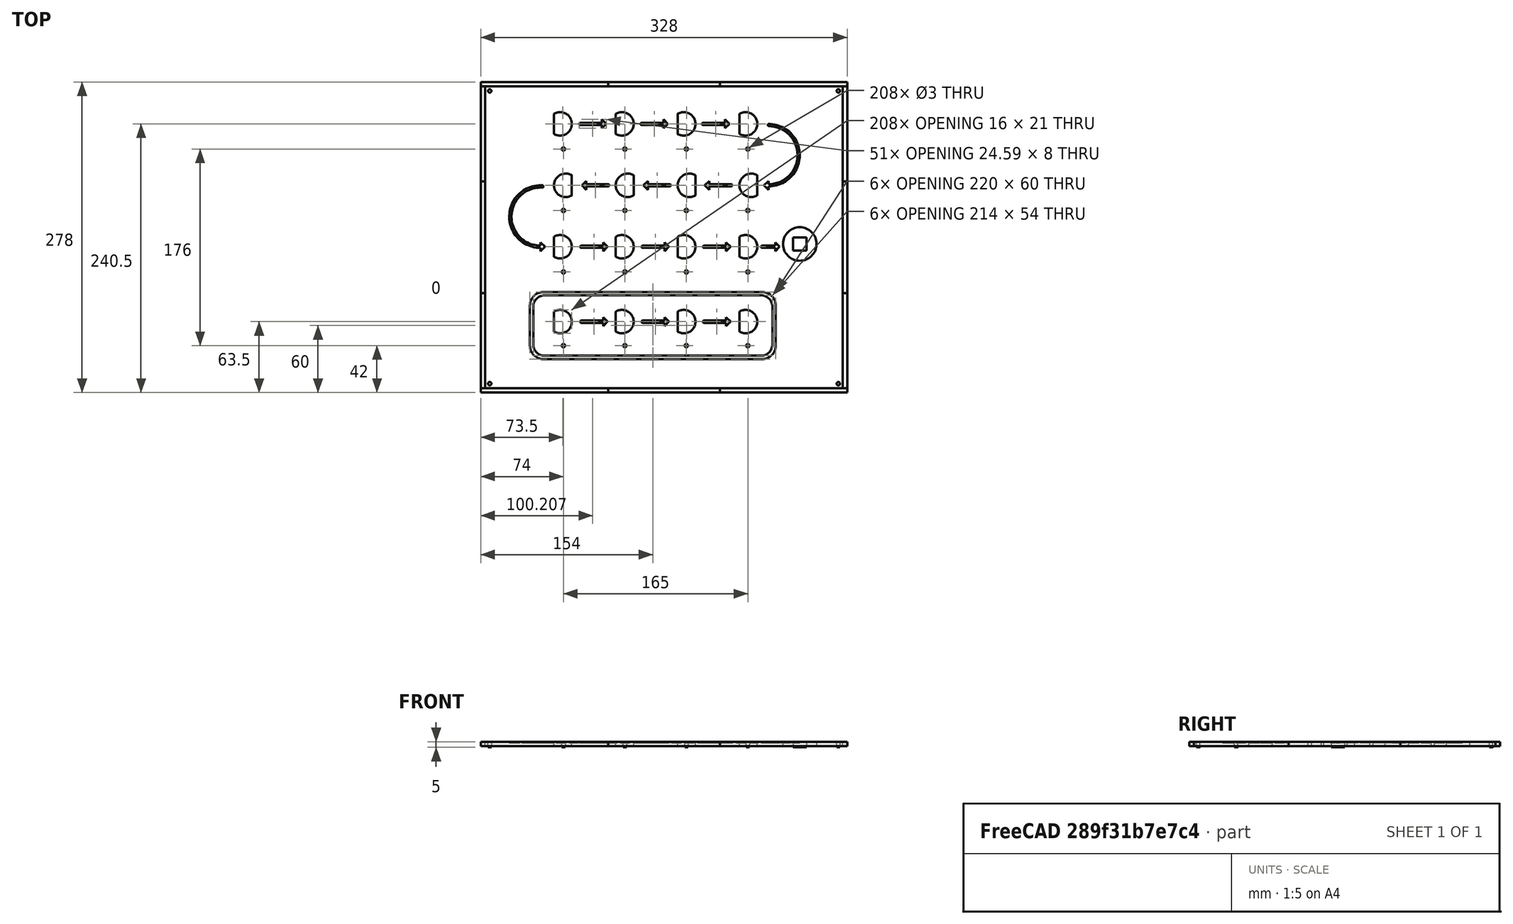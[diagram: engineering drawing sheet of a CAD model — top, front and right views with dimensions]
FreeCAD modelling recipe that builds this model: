
FCSTD DOCUMENT  (FreeCAD 0.14R3700 (Git))
Label: interFace-4mm (1)
License: CC-BY 3.0
LicenseURL: http://creativecommons.org/licenses/by/3.0/
objects: Sketcher::SketchObject×25, PartDesign::Pocket×17, PartDesign::Pad×8, Part::Cut×7, PartDesign::Fillet×7, PartDesign::LinearPattern×5, Part::Offset×4, Part::FeaturePython×4, Part::Box×3, Part::Fillet×2, Mesh::Feature×1
note: 107 computed .brp shape members not serialized (recipe doc carries the construction recipe); baked Part::Feature solids carry a one-line shape summary decoded from their .brp

FEATURE [Part::Box] Box  label="Cubo"
  Height = 4
  Length = 320
  Width = 270
FEATURE [Sketcher::SketchObject] Sketch004
  ExternalGeometry = -> [Box]
  Placement = pos=(0,0,4) rot=(0,0,1;0rad)
  Support = -> Box [Face6]
  sketch-geometry (4):
    g0: Circle CenterX=70 CenterY=214 CenterZ=0 NormalX=0 NormalY=0 NormalZ=1 Radius=1.5
    g1: Circle CenterX=125 CenterY=214 CenterZ=0 NormalX=0 NormalY=0 NormalZ=1 Radius=1.5
    g2: Circle CenterX=180 CenterY=214 CenterZ=0 NormalX=0 NormalY=0 NormalZ=1 Radius=1.5
    g3: Circle CenterX=235 CenterY=214 CenterZ=0 NormalX=0 NormalY=0 NormalZ=1 Radius=1.5
  constraints (12):
    c: Equal(g0,g1)
    c: Equal(g1,g3)
    c: Radius(g3) = 1.5
    c: DistanceY(g0,g-3) = 56
    c: DistanceY(g1,g-3) = 56
    c: DistanceX(g0,g-3) = -70
    c: DistanceX(g0,g1) = 55
    c: DistanceX(g1,g2) = 55
    c: DistanceX(g2,g3) = 55
    c: DistanceY(g3,g-3) = 56
    c: DistanceY(g2,g-3) = 56
    c: Equal(g2,g3)
FEATURE [Sketcher::SketchObject] Sketch008
  Placement = pos=(57,251.5,-1) rot=(0,0,-1;1.5708rad)
  sketch-geometry (2):
    g0: ArcOfCircle CenterX=15 CenterY=10 CenterZ=0 NormalX=0 NormalY=0 NormalZ=1 Radius=10 StartAngle=5.75959 EndAngle=9.94838
    g1: LineSegment StartX=6.33975 StartY=5 StartZ=0 EndX=23.6603 EndY=5 EndZ=0
  constraints (7):
    c: Radius(g0) = 10
    c: Horizontal(g1)
    c: PointOnObject(g0,g1)
    c: PointOnObject(g0,g1)
    c: Coincident(g1,g0)
    c: Coincident(g1,g0)
    c: DistanceY(g0,g0) = 5
FEATURE [PartDesign::Pad] Pad
  Length = 7
  Length2 = 100
  Placement = pos=(57,251.5,-1) rot=(0,0,-1;1.5708rad)
  Sketch = -> Sketch008
  Type = 0
FEATURE [Mesh::Feature] fichaLab3y  label="fichaLab3y4"
  Placement = pos=(127.33,181.5,-0.5) rot=(0,0,1;0rad)
FEATURE [PartDesign::Pocket] Pocket
  Length = 5
  Sketch = -> Sketch004
  Type = 0
FEATURE [PartDesign::LinearPattern] LinearPattern
  Direction = -> Sketch004 [V_Axis]
  Length = 110
  Occurrences = 3
  Originals = -> [Pocket]
  Reversed = true
FEATURE [Sketcher::SketchObject] Sketch005
  Placement = pos=(0,0,4) rot=(0,0,1;0rad)
  Support = -> LinearPattern [Face3]
  sketch-geometry (4):
    g0: Circle CenterX=70 CenterY=38 CenterZ=0 NormalX=0 NormalY=0 NormalZ=1 Radius=1.5
    g1: Circle CenterX=125 CenterY=38 CenterZ=0 NormalX=0 NormalY=0 NormalZ=1 Radius=1.5
    g2: Circle CenterX=180 CenterY=38 CenterZ=0 NormalX=0 NormalY=0 NormalZ=1 Radius=1.5
    g3: Circle CenterX=235 CenterY=38 CenterZ=0 NormalX=0 NormalY=0 NormalZ=1 Radius=1.5
  constraints (12):
    c: Equal(g0,g1)
    c: Equal(g1,g2)
    c: Equal(g2,g3)
    c: Radius(g0) = 1.5
    c: DistanceX(g-1,g0) = 70
    c: DistanceY(g-1,g0) = 38
    c: DistanceX(g0,g1) = 55
    c: DistanceY(g-1,g1) = 38
    c: DistanceX(g2,g1) = -55
    c: DistanceY(g-1,g2) = 38
    c: DistanceY(g-1,g3) = 38
    c: DistanceX(g3,g2) = -55
FEATURE [PartDesign::Pocket] Pocket001
  Length = 5
  Sketch = -> Sketch005
  Type = 0
FEATURE [Sketcher::SketchObject] Sketch007
  Placement = pos=(0,0,4) rot=(0,0,1;0rad)
  Support = -> Pocket001 [Face3]
  sketch-geometry (16):
    g0: Circle CenterX=67 CenterY=236.5 CenterZ=0 NormalX=0 NormalY=0 NormalZ=1 Radius=2
    g1: Circle CenterX=122.333 CenterY=236.5 CenterZ=0 NormalX=0 NormalY=0 NormalZ=1 Radius=2
    g2: Circle CenterX=177.667 CenterY=236.5 CenterZ=0 NormalX=0 NormalY=0 NormalZ=1 Radius=2
    g3: Circle CenterX=233 CenterY=236.5 CenterZ=0 NormalX=0 NormalY=0 NormalZ=1 Radius=2
    g4: Circle CenterX=72 CenterY=181.5 CenterZ=0 NormalX=0 NormalY=0 NormalZ=1 Radius=2
    g5: Circle CenterX=127.333 CenterY=181.5 CenterZ=0 NormalX=0 NormalY=0 NormalZ=1 Radius=2
    g6: Circle CenterX=182.667 CenterY=181.5 CenterZ=0 NormalX=0 NormalY=0 NormalZ=1 Radius=2
    g7: Circle CenterX=238 CenterY=181.5 CenterZ=0 NormalX=0 NormalY=0 NormalZ=1 Radius=2
    g8: Circle CenterX=67 CenterY=126.5 CenterZ=0 NormalX=0 NormalY=0 NormalZ=1 Radius=2
    g9: Circle CenterX=122.333 CenterY=126.5 CenterZ=0 NormalX=0 NormalY=0 NormalZ=1 Radius=2
    g10: Circle CenterX=177.667 CenterY=126.5 CenterZ=0 NormalX=0 NormalY=0 NormalZ=1 Radius=2
    g11: Circle CenterX=233 CenterY=126.5 CenterZ=0 NormalX=0 NormalY=0 NormalZ=1 Radius=2
    g12: Circle CenterX=67 CenterY=59.5 CenterZ=0 NormalX=0 NormalY=0 NormalZ=1 Radius=2
    g13: Circle CenterX=122.333 CenterY=59.5 CenterZ=0 NormalX=0 NormalY=0 NormalZ=1 Radius=2
    g14: Circle CenterX=177.667 CenterY=59.5 CenterZ=0 NormalX=0 NormalY=0 NormalZ=1 Radius=2
    g15: Circle CenterX=233 CenterY=59.5 CenterZ=0 NormalX=0 NormalY=0 NormalZ=1 Radius=2
  constraints (28):
    c: Equal(g0,g1)
    c: Equal(g1,g3)
    c: Equal(g3,g2)
    c: Radius(g0) = 2
    c: Equal(g7,g6)
    c: Equal(g6,g5)
    c: Equal(g5,g4)
    c: Radius(g7) = 2
    c: Equal(g11,g10)
    c: Equal(g10,g9)
    c: Equal(g9,g8)
    c: Radius(g11) = 2
    c: Equal(g15,g14)
    c: Equal(g14,g13)
    c: Equal(g13,g12)
    c: Radius(g15) = 2
    c: DistanceX(g0,g1) = 55.3333
    c: DistanceX(g1,g2) = 55.3334
    c: DistanceX(g2,g3) = 55.3333
    c: DistanceX(g4,g5) = 55.3333
    c: DistanceX(g5,g6) = 55.3334
    c: DistanceX(g6,g7) = 55.3333
    c: DistanceX(g8,g9) = 55.3333
    c: DistanceX(g9,g10) = 55.3334
    c: DistanceX(g10,g11) = 55.3333
    c: DistanceX(g12,g13) = 55.3333
    c: DistanceX(g13,g14) = 55.3333
    c: DistanceX(g14,g15) = 55.3334
FEATURE [PartDesign::Pocket] Pocket002
  Length = 5
  Sketch = -> Sketch007
  Type = 0
FEATURE [Part::Offset] Offset
  Fill = false
  Intersection = false
  Join = 0
  Mode = 0
  SelfIntersection = false
  Source = -> Pad
  Value = 0.5
FEATURE [Part::FeaturePython] Array  # Draft array (typed FeaturePython)
  Angle = 360
  ArrayType = 0
  Axis = (0,0,1)
  Base = -> Offset
  Center = (0,0,0)
  IntervalX = (55.33,0,0)
  IntervalY = (0,1,0)
  IntervalZ = (0,0,1)
  NumberPolar = 1
  NumberX = 4
  NumberY = 1
  NumberZ = 1
FEATURE [Part::Cut] Cut
  Base = -> Pocket002
  Tool = -> Array
FEATURE [Sketcher::SketchObject] Sketch
  Placement = pos=(57,141.5,-1) rot=(0,0,-1;1.5708rad)
  sketch-geometry (2):
    g0: ArcOfCircle CenterX=15 CenterY=10 CenterZ=0 NormalX=0 NormalY=0 NormalZ=1 Radius=10 StartAngle=5.75959 EndAngle=9.94838
    g1: LineSegment StartX=6.33975 StartY=5 StartZ=0 EndX=23.6603 EndY=5 EndZ=0
  constraints (7):
    c: Radius(g0) = 10
    c: Horizontal(g1)
    c: PointOnObject(g0,g1)
    c: PointOnObject(g0,g1)
    c: Coincident(g1,g0)
    c: Coincident(g1,g0)
    c: DistanceY(g0,g0) = 5
FEATURE [PartDesign::Pad] Pad001
  Length = 7
  Length2 = 100
  Placement = pos=(57,141.5,-1) rot=(0,0,-1;1.5708rad)
  Sketch = -> Sketch
  Type = 0
FEATURE [Part::Offset] Offset001
  Fill = false
  Intersection = false
  Join = 0
  Mode = 0
  SelfIntersection = false
  Source = -> Pad001
  Value = 0.5
FEATURE [Part::FeaturePython] Array001  # Draft array (typed FeaturePython)
  Angle = 360
  ArrayType = 0
  Axis = (0,0,1)
  Base = -> Offset001
  Center = (0,0,0)
  IntervalX = (55.33,0,0)
  IntervalY = (0,1,0)
  IntervalZ = (0,0,1)
  NumberPolar = 1
  NumberX = 4
  NumberY = 1
  NumberZ = 1
FEATURE [Part::Cut] Cut001
  Base = -> Cut
  Tool = -> Array001
FEATURE [Sketcher::SketchObject] Sketch009
  Placement = pos=(57,74.5,-1) rot=(0,0,-1;1.5708rad)
  sketch-geometry (2):
    g0: ArcOfCircle CenterX=15 CenterY=10 CenterZ=0 NormalX=0 NormalY=0 NormalZ=1 Radius=10 StartAngle=5.75959 EndAngle=9.94838
    g1: LineSegment StartX=6.33975 StartY=5 StartZ=0 EndX=23.6603 EndY=5 EndZ=0
  constraints (7):
    c: Radius(g0) = 10
    c: Horizontal(g1)
    c: PointOnObject(g0,g1)
    c: PointOnObject(g0,g1)
    c: Coincident(g1,g0)
    c: Coincident(g1,g0)
    c: DistanceY(g0,g0) = 5
FEATURE [PartDesign::Pad] Pad002
  Length = 7
  Length2 = 100
  Placement = pos=(57,74.5,-1) rot=(0,0,-1;1.5708rad)
  Sketch = -> Sketch009
  Type = 0
FEATURE [Part::Offset] Offset002
  Fill = false
  Intersection = false
  Join = 0
  Mode = 0
  SelfIntersection = false
  Source = -> Pad002
  Value = 0.5
FEATURE [Part::FeaturePython] Array002  # Draft array (typed FeaturePython)
  Angle = 360
  ArrayType = 0
  Axis = (0,0,1)
  Base = -> Offset002
  Center = (0,0,0)
  IntervalX = (55.33,0,0)
  IntervalY = (0,1,0)
  IntervalZ = (0,0,1)
  NumberPolar = 1
  NumberX = 4
  NumberY = 1
  NumberZ = 1
FEATURE [Part::Cut] Cut002
  Base = -> Cut001
  Tool = -> Array002
FEATURE [Sketcher::SketchObject] Sketch010
  Placement = pos=(82,166.5,-1) rot=(0,0,1;1.5708rad)
  sketch-geometry (2):
    g0: ArcOfCircle CenterX=15 CenterY=10 CenterZ=0 NormalX=0 NormalY=0 NormalZ=1 Radius=10 StartAngle=5.75959 EndAngle=9.94838
    g1: LineSegment StartX=6.33975 StartY=5 StartZ=0 EndX=23.6603 EndY=5 EndZ=0
  constraints (7):
    c: Radius(g0) = 10
    c: Horizontal(g1)
    c: PointOnObject(g0,g1)
    c: PointOnObject(g0,g1)
    c: Coincident(g1,g0)
    c: Coincident(g1,g0)
    c: DistanceY(g0,g0) = 5
FEATURE [PartDesign::Pad] Pad003
  Length = 7
  Length2 = 100
  Placement = pos=(82,166.5,-1) rot=(0,0,1;1.5708rad)
  Sketch = -> Sketch010
  Type = 0
FEATURE [Part::Offset] Offset003
  Fill = false
  Intersection = false
  Join = 0
  Mode = 0
  SelfIntersection = false
  Source = -> Pad003
  Value = 0.5
FEATURE [Part::FeaturePython] Array003  # Draft array (typed FeaturePython)
  Angle = 360
  ArrayType = 0
  Axis = (0,0,1)
  Base = -> Offset003
  Center = (0,0,0)
  IntervalX = (55.33,0,0)
  IntervalY = (0,1,0)
  IntervalZ = (0,0,1)
  NumberPolar = 1
  NumberX = 4
  NumberY = 1
  NumberZ = 1
FEATURE [Part::Cut] Cut003
  Base = -> Cut002
  Tool = -> Array003
FEATURE [Sketcher::SketchObject] Sketch011
  ExternalGeometry = -> [Cut003]
  Placement = pos=(0,0,4) rot=(0,0,1;0rad)
  Support = -> Cut003 [Face3]
  sketch-geometry (4):
    g0: LineSegment StartX=275.5 StartY=135 StartZ=0 EndX=287.5 EndY=135 EndZ=0
    g1: LineSegment StartX=287.5 StartY=135 StartZ=0 EndX=287.5 EndY=123 EndZ=0
    g2: LineSegment StartX=287.5 StartY=123 StartZ=0 EndX=275.5 EndY=123 EndZ=0
    g3: LineSegment StartX=275.5 StartY=123 StartZ=0 EndX=275.5 EndY=135 EndZ=0
  constraints (14):
    c: Coincident(g0,g1)
    c: Coincident(g1,g2)
    c: Coincident(g2,g3)
    c: Coincident(g3,g0)
    c: Horizontal(g0)
    c: Horizontal(g2)
    c: Vertical(g1)
    c: Vertical(g3)
    c: Equal(g0,g2)
    c: Equal(g2,g1)
    c: Equal(g1,g3)
    c: DistanceX(g0) = 12
    c: DistanceX(g1,g-3) = 32.5
    c: DistanceY(g1,g-3) = -123
FEATURE [PartDesign::Pocket] Pocket003  label="interFace-4mm(1)"
  Length = 5
  Sketch = -> Sketch011
  Type = 0
FEATURE [Sketcher::SketchObject] Sketch012
  Placement = pos=(0,0,4) rot=(0,0,1;0rad)
  Support = -> Pocket003 [Face3]
  sketch-geometry (1):
    g0: Circle CenterX=281.5 CenterY=129 CenterZ=0 NormalX=0 NormalY=0 NormalZ=1 Radius=15
  constraints (1):
    c: Radius(g0) = 15
FEATURE [PartDesign::Pocket] Pocket004
  Length = 5
  Sketch = -> Sketch012
  Type = 0
FEATURE [Part::Box] Box001  label="Cubo001"
  Height = 10
  Length = 214
  Placement = pos=(43,29,-2) rot=(0,0,1;0rad)
  Width = 54
FEATURE [Part::Box] Box002  label="Cubo002"
  Height = 10
  Length = 220
  Placement = pos=(40,26,-2) rot=(0,0,1;0rad)
  Width = 60
FEATURE [Part::Cut] Cut004
  Base = -> Box002
  Tool = -> Box001
FEATURE [Part::Fillet] Fillet
  Base = -> Cut004
  Edges = 4 edges r=10: [Edge21,Edge22,Edge23,Edge24]
FEATURE [Part::Fillet] Fillet001
  Base = -> Fillet
  Edges = 4 edges r=12: [Edge29,Edge30,Edge33,Edge35]
  Placement = pos=(0,0,5) rot=(0,0,1;0rad)
FEATURE [Part::Cut] Cut005
  Base = -> Pocket004
  Tool = -> Fillet001
FEATURE [Sketcher::SketchObject] Sketch013
  ExternalGeometry = -> [Cut005]
  Placement = pos=(0,0,4) rot=(0,0,1;0rad)
  Support = -> Cut005 [Face3]
  sketch-geometry (9):
    g0: LineSegment StartX=84.5 StartY=235.5 StartZ=0 EndX=104.5 EndY=235.5 EndZ=0
    g1: LineSegment StartX=104.5 StartY=235.5 StartZ=0 EndX=104.5 EndY=232.5 EndZ=0
    g2: LineSegment StartX=104.5 StartY=232.5 StartZ=0 EndX=108.5 EndY=236.5 EndZ=0
    g3: LineSegment StartX=108.5 StartY=236.5 StartZ=0 EndX=104.5 EndY=240.5 EndZ=0
    g4: LineSegment StartX=104.5 StartY=240.5 StartZ=0 EndX=104.5 EndY=237.5 EndZ=0
    g5: LineSegment StartX=104.5 StartY=237.5 StartZ=0 EndX=84.5 EndY=237.5 EndZ=0
    g6: LineSegment StartX=84.5 StartY=237.5 StartZ=0 EndX=83.5 EndY=236.5 EndZ=0
    g7: LineSegment StartX=83.5 StartY=236.5 StartZ=0 EndX=84.5 EndY=235.5 EndZ=0
    g8: LineSegment [constr] StartX=83.5 StartY=236.5 StartZ=0 EndX=108.5 EndY=236.5 EndZ=0
  constraints (28):
    c: Horizontal(g0)
    c: Coincident(g0,g1)
    c: Vertical(g1)
    c: Coincident(g1,g2)
    c: Coincident(g2,g3)
    c: Coincident(g3,g4)
    c: Coincident(g4,g5)
    c: Horizontal(g5)
    c: DistanceX(g0) = 20
    c: Equal(g5,g0)
    c: DistanceX(g2,g0) = -24
    c: DistanceY(g2,g5) = 1
    c: Equal(g1,g4)
    c: Vertical(g4)
    c: Angle(g3,g2) = 1.5708
    c: DistanceX(g0,g-3) = -23
    c: Coincident(g5,g6)
    c: Coincident(g6,g7)
    c: Coincident(g7,g0)
    c: Coincident(g8,g6)
    c: Coincident(g8,g2)
    c: Horizontal(g8)
    c: Equal(g6,g7)
    c: Equal(g0,g5)
    c: Equal(g2,g3)
    c: Equal(g1,g4)
    c: Symmetric(g-3,g-3,g8)
    c: DistanceX(g6,g0) = 1
FEATURE [PartDesign::Pocket] Pocket005
  Length = 1
  Sketch = -> Sketch013
  Type = 0
FEATURE [PartDesign::LinearPattern] LinearPattern001
  Direction = -> Sketch013 [H_Axis]
  Length = 110
  Occurrences = 3
  Originals = -> [Pocket005]
FEATURE [Part::Cut] Cut006
  Base = -> Pocket004
  Tool = -> Fillet001
FEATURE [PartDesign::Fillet] Fillet002
  Base = -> LinearPattern001 [Edge239,Edge234,Edge218]
  Radius = 1
FEATURE [Sketcher::SketchObject] Sketch014
  ExternalGeometry = -> [Fillet002]
  Placement = pos=(0,0,4) rot=(0,0,1;0rad)
  Support = -> Fillet002 [Face1]
  sketch-geometry (9):
    g0: LineSegment StartX=220.49 StartY=182.5 StartZ=0 EndX=200.49 EndY=182.5 EndZ=0
    g1: LineSegment StartX=200.49 StartY=182.5 StartZ=0 EndX=200.49 EndY=185.5 EndZ=0
    g2: LineSegment StartX=200.49 StartY=185.5 StartZ=0 EndX=196.49 EndY=181.5 EndZ=0
    g3: LineSegment StartX=196.49 StartY=181.5 StartZ=0 EndX=200.49 EndY=177.5 EndZ=0
    g4: LineSegment StartX=200.49 StartY=177.5 StartZ=0 EndX=200.49 EndY=180.5 EndZ=0
    g5: LineSegment StartX=200.49 StartY=180.5 StartZ=0 EndX=220.49 EndY=180.5 EndZ=0
    g6: LineSegment StartX=220.49 StartY=180.5 StartZ=0 EndX=221.49 EndY=181.5 EndZ=0
    g7: LineSegment StartX=221.49 StartY=181.5 StartZ=0 EndX=220.49 EndY=182.5 EndZ=0
    g8: LineSegment [constr] StartX=196.49 StartY=181.5 StartZ=0 EndX=221.49 EndY=181.5 EndZ=0
  constraints (29):
    c: Horizontal(g0)
    c: Coincident(g0,g1)
    c: Vertical(g1)
    c: Coincident(g1,g2)
    c: Coincident(g2,g3)
    c: Coincident(g3,g4)
    c: Vertical(g4)
    c: Coincident(g4,g5)
    c: Horizontal(g5)
    c: Coincident(g5,g6)
    c: Coincident(g6,g7)
    c: Coincident(g7,g0)
    c: Equal(g1,g4)
    c: Equal(g0,g5)
    c: Equal(g7,g6)
    c: Coincident(g8,g2)
    c: Coincident(g8,g6)
    c: Horizontal(g8)
    c: DistanceX(g8) = 25
    c: DistanceX(g2,g0) = 24
    c: Equal(g0,g5)
    c: DistanceX(g0) = -20
    c: Angle(g3,g2) = 1.5708
    c: DistanceY(g0,g5) = -2
    c: Angle(g7,g6) = 1.5708
    c: Equal(g2,g3)
    c: Equal(g1,g4)
    c: Symmetric(g-3,g-3,g8)
    c: DistanceX(g6,g-3) = 22
FEATURE [PartDesign::Pocket] Pocket006
  Length = 1
  Sketch = -> Sketch014
  Type = 0
FEATURE [PartDesign::LinearPattern] LinearPattern002
  Direction = -> Sketch014 [H_Axis]
  Length = 110
  Occurrences = 3
  Originals = -> [Pocket006]
  Reversed = true
FEATURE [PartDesign::Fillet] Fillet003
  Base = -> LinearPattern002 [Edge173,Edge168,Edge152]
  Radius = 1
FEATURE [Sketcher::SketchObject] Sketch015
  ExternalGeometry = -> [Fillet003]
  Placement = pos=(0,0,4) rot=(0,0,1;0rad)
  Support = -> Fillet003 [Face1]
  sketch-geometry (9):
    g0: LineSegment StartX=85.5 StartY=127.5 StartZ=0 EndX=105.5 EndY=127.5 EndZ=0
    g1: LineSegment StartX=105.5 StartY=127.5 StartZ=0 EndX=105.5 EndY=130.5 EndZ=0
    g2: LineSegment StartX=105.5 StartY=130.5 StartZ=0 EndX=109.5 EndY=126.5 EndZ=0
    g3: LineSegment StartX=109.5 StartY=126.5 StartZ=0 EndX=105.5 EndY=122.5 EndZ=0
    g4: LineSegment StartX=105.5 StartY=122.5 StartZ=0 EndX=105.5 EndY=125.5 EndZ=0
    g5: LineSegment StartX=105.5 StartY=125.5 StartZ=0 EndX=85.5 EndY=125.5 EndZ=0
    g6: LineSegment StartX=85.5 StartY=125.5 StartZ=0 EndX=84.5 EndY=126.5 EndZ=0
    g7: LineSegment StartX=84.5 StartY=126.5 StartZ=0 EndX=85.5 EndY=127.5 EndZ=0
    g8: LineSegment [constr] StartX=84.5 StartY=126.5 StartZ=0 EndX=109.5 EndY=126.5 EndZ=0
  constraints (26):
    c: Horizontal(g0)
    c: Coincident(g0,g1)
    c: Vertical(g1)
    c: Coincident(g1,g2)
    c: Coincident(g2,g3)
    c: Coincident(g3,g4)
    c: Vertical(g4)
    c: Coincident(g4,g5)
    c: Horizontal(g5)
    c: Coincident(g5,g6)
    c: Coincident(g6,g7)
    c: Coincident(g7,g0)
    c: Coincident(g8,g6)
    c: Coincident(g8,g2)
    c: Horizontal(g8)
    c: Equal(g0,g5)
    c: Equal(g1,g4)
    c: Equal(g2,g3)
    c: Equal(g7,g6)
    c: Angle(g2,g3) = 1.5708
    c: DistanceX(g0) = 20
    c: Angle(g6,g7) = 1.5708
    c: DistanceX(g8) = 25
    c: DistanceY(g4,g0) = 2
    c: Symmetric(g-3,g-3,g8)
    c: DistanceX(g5,g-3) = -24
FEATURE [PartDesign::Pocket] Pocket007
  Length = 1
  Sketch = -> Sketch015
  Type = 0
FEATURE [PartDesign::LinearPattern] LinearPattern003
  Direction = -> Sketch015 [H_Axis]
  Length = 110
  Occurrences = 3
  Originals = -> [Pocket007]
FEATURE [PartDesign::Fillet] Fillet004
  Base = -> LinearPattern003 [Edge419,Edge435,Edge451]
  Radius = 1
FEATURE [Sketcher::SketchObject] Sketch016
  ExternalGeometry = -> [Fillet004]
  Placement = pos=(0,0,4) rot=(0,0,1;0rad)
  Support = -> Fillet004 [Face1]
  sketch-geometry (9):
    g0: LineSegment StartX=247.49 StartY=127.5 StartZ=0 EndX=259.49 EndY=127.5 EndZ=0
    g1: LineSegment StartX=259.49 StartY=127.5 StartZ=0 EndX=259.49 EndY=130.5 EndZ=0
    g2: LineSegment StartX=259.49 StartY=130.5 StartZ=0 EndX=263.49 EndY=126.5 EndZ=0
    g3: LineSegment StartX=263.49 StartY=126.5 StartZ=0 EndX=259.49 EndY=122.5 EndZ=0
    g4: LineSegment StartX=259.49 StartY=122.5 StartZ=0 EndX=259.49 EndY=125.5 EndZ=0
    g5: LineSegment StartX=259.49 StartY=125.5 StartZ=0 EndX=247.49 EndY=125.5 EndZ=0
    g6: LineSegment StartX=247.49 StartY=125.5 StartZ=0 EndX=246.49 EndY=126.5 EndZ=0
    g7: LineSegment StartX=246.49 StartY=126.5 StartZ=0 EndX=247.49 EndY=127.5 EndZ=0
    g8: LineSegment [constr] StartX=246.49 StartY=126.5 StartZ=0 EndX=263.49 EndY=126.5 EndZ=0
  constraints (26):
    c: Horizontal(g0)
    c: Coincident(g0,g1)
    c: Vertical(g1)
    c: Coincident(g1,g2)
    c: Coincident(g2,g3)
    c: Coincident(g3,g4)
    c: Vertical(g4)
    c: Coincident(g4,g5)
    c: Coincident(g5,g6)
    c: Coincident(g6,g7)
    c: Coincident(g7,g0)
    c: Coincident(g8,g6)
    c: Coincident(g8,g2)
    c: Horizontal(g8)
    c: Angle(g6,g7) = 1.5708
    c: Angle(g2,g3) = 1.5708
    c: Equal(g5,g0)
    c: Horizontal(g5)
    c: DistanceY(g0,g4) = -2
    c: Equal(g1,g4)
    c: Equal(g2,g3)
    c: DistanceX(g8) = 17
    c: DistanceX(g0,g6) = -1
    c: DistanceX(g0) = 12
    c: Symmetric(g-3,g-3,g8)
    c: DistanceX(g5,g-3) = -20
FEATURE [PartDesign::Pocket] Pocket008
  Length = 1
  Sketch = -> Sketch016
  Type = 0
FEATURE [PartDesign::Fillet] Fillet005
  Base = -> Pocket008 [Edge484]
  Radius = 1
FEATURE [Sketcher::SketchObject] Sketch017
  ExternalGeometry = -> [Fillet005]
  Placement = pos=(0,0,4) rot=(0,0,1;0rad)
  Support = -> Fillet005 [Face205]
  sketch-geometry (9):
    g0: LineSegment StartX=85.5 StartY=60.5 StartZ=0 EndX=105.5 EndY=60.5 EndZ=0
    g1: LineSegment StartX=105.5 StartY=60.5 StartZ=0 EndX=105.5 EndY=63.5 EndZ=0
    g2: LineSegment StartX=105.5 StartY=63.5 StartZ=0 EndX=109.5 EndY=59.5 EndZ=0
    g3: LineSegment StartX=109.5 StartY=59.5 StartZ=0 EndX=105.5 EndY=55.5 EndZ=0
    g4: LineSegment StartX=105.5 StartY=55.5 StartZ=0 EndX=105.5 EndY=58.5 EndZ=0
    g5: LineSegment StartX=105.5 StartY=58.5 StartZ=0 EndX=85.5 EndY=58.5 EndZ=0
    g6: LineSegment StartX=85.5 StartY=58.5 StartZ=0 EndX=84.5 EndY=59.5 EndZ=0
    g7: LineSegment StartX=84.5 StartY=59.5 StartZ=0 EndX=85.5 EndY=60.5 EndZ=0
    g8: LineSegment [constr] StartX=84.5 StartY=59.5 StartZ=0 EndX=109.5 EndY=59.5 EndZ=0
  constraints (26):
    c: Horizontal(g0)
    c: Coincident(g0,g1)
    c: Vertical(g1)
    c: Coincident(g1,g2)
    c: Coincident(g2,g3)
    c: Coincident(g3,g4)
    c: Vertical(g4)
    c: Coincident(g4,g5)
    c: Horizontal(g5)
    c: Coincident(g5,g6)
    c: Coincident(g6,g7)
    c: Coincident(g7,g0)
    c: Coincident(g8,g6)
    c: Coincident(g8,g2)
    c: Horizontal(g8)
    c: Equal(g0,g5)
    c: Equal(g2,g3)
    c: Equal(g1,g4)
    c: Equal(g7,g6)
    c: Angle(g6,g7) = 1.5708
    c: Angle(g2,g3) = 1.5708
    c: DistanceX(g8) = 25
    c: DistanceX(g0,g6) = -1
    c: DistanceX(g0) = 20
    c: Symmetric(g-3,g-3,g8)
    c: DistanceX(g5,g-3) = -24
FEATURE [PartDesign::Pocket] Pocket009
  Length = 1
  Sketch = -> Sketch017
  Type = 0
FEATURE [PartDesign::LinearPattern] LinearPattern004
  Direction = -> Sketch017 [H_Axis]
  Length = 110
  Occurrences = 3
  Originals = -> [Pocket009]
FEATURE [PartDesign::Fillet] Fillet006
  Base = -> LinearPattern004 [Edge615,Edge631,Edge647]
  Radius = 1
FEATURE [Sketcher::SketchObject] Sketch018
  ExternalGeometry = -> [Fillet006]
  Placement = pos=(0,0,4) rot=(0,0,1;0rad)
  Support = -> Fillet006 [Face135]
  sketch-geometry (11):
    g0: LineSegment StartX=253.49 StartY=182.5 StartZ=0 EndX=253.49 EndY=185.5 EndZ=0
    g1: LineSegment StartX=253.49 StartY=185.5 StartZ=0 EndX=249.49 EndY=181.5 EndZ=0
    g2: LineSegment StartX=249.49 StartY=181.5 StartZ=0 EndX=253.49 EndY=177.5 EndZ=0
    g3: LineSegment StartX=253.49 StartY=177.5 StartZ=0 EndX=253.49 EndY=180.5 EndZ=0
    g4: LineSegment [constr] StartX=249.49 StartY=181.5 StartZ=0 EndX=269.239 EndY=181.5 EndZ=0
    g5: ArcOfCircle CenterX=253.49 CenterY=208.5 CenterZ=0 NormalX=0 NormalY=0 NormalZ=1 Radius=26 StartAngle=4.71239 EndAngle=7.85045
    g6: ArcOfCircle CenterX=253.49 CenterY=208.5 CenterZ=0 NormalX=0 NormalY=0 NormalZ=1 Radius=28 StartAngle=4.71239 EndAngle=7.85727
    g7: LineSegment StartX=253.398 StartY=236.5 StartZ=0 EndX=252.49 EndY=235.408 EndZ=0
    g8: LineSegment StartX=252.49 StartY=235.408 StartZ=0 EndX=253.582 EndY=234.5 EndZ=0
    g9: LineSegment [constr] StartX=253.398 StartY=236.5 StartZ=0 EndX=253.582 EndY=234.5 EndZ=0
    g10: LineSegment [constr] StartX=252.49 StartY=235.408 StartZ=0 EndX=253.49 EndY=235.5 EndZ=0
  constraints (32):
    c: Vertical(g0)
    c: Coincident(g0,g1)
    c: Coincident(g1,g2)
    c: Coincident(g2,g3)
    c: Angle(g2,g1) = 1.5708
    c: Equal(g0,g3)
    c: Equal(g1,g2)
    c: Coincident(g4,g1)
    c: Horizontal(g4)
    c: Symmetric(g-4,g-4,g4)
    c: DistanceX(g-4,g1) = 6
    c: DistanceX(g1,g0) = 4
    c: Symmetric(g0,g2,g4)
    c: Vertical(g3)
    c: DistanceY(g0) = 3
    c: Coincident(g5,g0)
    c: Coincident(g6,g5)
    c: Coincident(g6,g3)
    c: Coincident(g7,g6)
    c: Coincident(g8,g7)
    c: Coincident(g8,g5)
    c: Coincident(g9,g6)
    c: Coincident(g9,g5)
    c: Coincident(g10,g7)
    c: PointOnObject(g10,g9)
    c: Symmetric(g5,g6,g10)
    c: Equal(g7,g8)
    c: Angle(g8,g7) = 1.5708
    c: Radius(g5) = 26
    c: Radius(g6) = 28
    c: DistanceX(g4) = 19.7495
    c: DistanceX(g7,g-3) = -25
FEATURE [PartDesign::Pocket] Pocket010
  Length = 1
  Sketch = -> Sketch018
  Type = 0
FEATURE [PartDesign::Fillet] Fillet007
  Base = -> Pocket010 [Edge512]
  Radius = 1
FEATURE [Sketcher::SketchObject] Sketch019
  ExternalGeometry = -> [Fillet007]
  Placement = pos=(0,0,4) rot=(0,0,1;0rad)
  Support = -> Fillet007 [Face1]
  sketch-geometry (11):
    g0: LineSegment StartX=49.5 StartY=127.5 StartZ=0 EndX=49.5 EndY=130.5 EndZ=0
    g1: LineSegment StartX=49.5 StartY=130.5 StartZ=0 EndX=53.5 EndY=126.5 EndZ=0
    g2: LineSegment StartX=53.5 StartY=126.5 StartZ=0 EndX=49.5 EndY=122.5 EndZ=0
    g3: LineSegment StartX=49.5 StartY=122.5 StartZ=0 EndX=49.5 EndY=125.5 EndZ=0
    g4: LineSegment [constr] StartX=53.5 StartY=126.5 StartZ=0 EndX=39.2166 EndY=126.5 EndZ=0
    g5: ArcOfCircle CenterX=49.5 CenterY=153.5 CenterZ=0 NormalX=0 NormalY=0 NormalZ=1 Radius=26 StartAngle=1.4938 EndAngle=4.71239
    g6: ArcOfCircle CenterX=49.5 CenterY=153.5 CenterZ=0 NormalX=0 NormalY=0 NormalZ=1 Radius=28 StartAngle=1.49952 EndAngle=4.71239
    g7: LineSegment StartX=51.4941 StartY=181.429 StartZ=0 EndX=52.5 EndY=180.429 EndZ=0
    g8: LineSegment StartX=52.5 StartY=180.429 StartZ=0 EndX=51.5 EndY=179.423 EndZ=0
    g9: LineSegment [constr] StartX=51.4941 StartY=181.429 StartZ=0 EndX=51.5 EndY=179.423 EndZ=0
    g10: LineSegment [constr] StartX=52.5 StartY=180.429 StartZ=0 EndX=51.497 EndY=180.426 EndZ=0
  constraints (34):
    c: Vertical(g0)
    c: Coincident(g0,g1)
    c: Coincident(g1,g2)
    c: Coincident(g2,g3)
    c: Vertical(g3)
    c: Coincident(g4,g1)
    c: Horizontal(g4)
    c: Equal(g3,g0)
    c: Equal(g1,g2)
    c: Angle(g1,g2) = 1.5708
    c: Symmetric(g-3,g-3,g4)
    c: DistanceY(g3) = 3
    c: DistanceX(g0,g1) = 4
    c: DistanceX(g3,g1) = 4
    c: Coincident(g5,g0)
    c: Coincident(g6,g5)
    c: Coincident(g6,g3)
    c: Radius(g5) = 26
    c: DistanceX(g1,g-3) = 8
    c: Radius(g6) = 28
    c: Coincident(g7,g6)
    c: Coincident(g8,g7)
    c: Coincident(g8,g5)
    c: Angle(g7,g8) = 1.5708
    c: DistanceX(g5,g7) = 1
    c: Equal(g7,g8)
    c: DistanceX(g7,g-4) = 25
    c: Coincident(g9,g6)
    c: Coincident(g9,g5)
    c: Coincident(g10,g7)
    c: PointOnObject(g10,g9)
    c: Angle(g7,g10) = 0.785398
    c: Symmetric(g5,g6,g10)
    c: DistanceY(g7,g-4) = -7.58916
FEATURE [PartDesign::Pocket] Pocket011
  Length = 1
  Sketch = -> Sketch019
  Type = 0
FEATURE [PartDesign::Fillet] Fillet008
  Base = -> Pocket011 [Edge541]
  Radius = 1
FEATURE [Sketcher::SketchObject] Sketch020
  ExternalGeometry = -> [Fillet008]
  Placement = pos=(0,270,0) rot=(0,0.707107,0.707107;3.14159rad)
  Support = -> Fillet008 [Face126]
  sketch-geometry (4):
    g0: LineSegment StartX=-324 StartY=4 StartZ=0 EndX=4 EndY=4 EndZ=0
    g1: LineSegment StartX=4 StartY=4 StartZ=0 EndX=4 EndY=0 EndZ=0
    g2: LineSegment StartX=4 StartY=0 StartZ=0 EndX=-324 EndY=0 EndZ=0
    g3: LineSegment StartX=-324 StartY=0 StartZ=0 EndX=-324 EndY=4 EndZ=0
  constraints (14):
    c: Coincident(g0,g1)
    c: Coincident(g1,g2)
    c: Coincident(g2,g3)
    c: Coincident(g3,g0)
    c: Horizontal(g0)
    c: Horizontal(g2)
    c: Vertical(g1)
    c: Vertical(g3)
    c: Equal(g3,g1)
    c: Equal(g2,g0)
    c: DistanceX(g0) = 328
    c: DistanceY(g3) = 4
    c: DistanceX(g2,g-3) = 4
    c: DistanceY(g2,g-3) = 0
FEATURE [PartDesign::Pad] Pad004
  Length = 4
  Length2 = 100
  Sketch = -> Sketch020
  Type = 0
FEATURE [Sketcher::SketchObject] Sketch021
  ExternalGeometry = -> [Pad004]
  Placement = pos=(0,0,0) rot=(1,0,0;1.5708rad)
  Support = -> Pad004 [Face2]
  sketch-geometry (4):
    g0: LineSegment StartX=-4 StartY=4 StartZ=0 EndX=324 EndY=4 EndZ=0
    g1: LineSegment StartX=324 StartY=4 StartZ=0 EndX=324 EndY=0 EndZ=0
    g2: LineSegment StartX=324 StartY=0 StartZ=0 EndX=-4 EndY=0 EndZ=0
    g3: LineSegment StartX=-4 StartY=0 StartZ=0 EndX=-4 EndY=4 EndZ=0
  constraints (14):
    c: Coincident(g0,g1)
    c: Coincident(g1,g2)
    c: Coincident(g2,g3)
    c: Coincident(g3,g0)
    c: Horizontal(g0)
    c: Horizontal(g2)
    c: Vertical(g1)
    c: Vertical(g3)
    c: Equal(g0,g2)
    c: Equal(g1,g3)
    c: DistanceX(g0) = 328
    c: DistanceY(g3) = 4
    c: DistanceX(g-1,g2) = -4
    c: DistanceY(g-1,g2) = 0
FEATURE [PartDesign::Pad] Pad005
  Length = 4
  Length2 = 100
  Sketch = -> Sketch021
  Type = 0
FEATURE [Sketcher::SketchObject] Sketch022
  ExternalGeometry = -> [Pad005]
  Placement = pos=(0,0,0) rot=(0.57735,-0.57735,-0.57735;2.0944rad)
  Support = -> Pad005 [Face6]
  sketch-geometry (4):
    g0: LineSegment StartX=-270 StartY=0 StartZ=0 EndX=0 EndY=0 EndZ=0
    g1: LineSegment StartX=0 StartY=0 StartZ=0 EndX=0 EndY=4 EndZ=0
    g2: LineSegment StartX=0 StartY=4 StartZ=0 EndX=-270 EndY=4 EndZ=0
    g3: LineSegment StartX=-270 StartY=4 StartZ=0 EndX=-270 EndY=0 EndZ=0
  constraints (11):
    c: Coincident(g0,g1)
    c: Coincident(g1,g2)
    c: Coincident(g2,g3)
    c: Coincident(g3,g0)
    c: Horizontal(g0)
    c: Horizontal(g2)
    c: Vertical(g1)
    c: Vertical(g3)
    c: Coincident(g0,g-3)
    c: DistanceX(g2) = -270
    c: DistanceY(g3) = -4
FEATURE [PartDesign::Pad] Pad006
  Length = 4
  Length2 = 100
  Sketch = -> Sketch022
  Type = 0
FEATURE [Sketcher::SketchObject] Sketch023
  Placement = pos=(320,0,0) rot=(0.57735,0.57735,0.57735;2.0944rad)
  Support = -> Pad006 [Face1]
  sketch-geometry (4):
    g0: LineSegment StartX=0 StartY=0 StartZ=0 EndX=270 EndY=0 EndZ=0
    g1: LineSegment StartX=270 StartY=0 StartZ=0 EndX=270 EndY=4 EndZ=0
    g2: LineSegment StartX=270 StartY=4 StartZ=0 EndX=0 EndY=4 EndZ=0
    g3: LineSegment StartX=0 StartY=4 StartZ=0 EndX=0 EndY=0 EndZ=0
  constraints (11):
    c: Coincident(g0,g1)
    c: Coincident(g1,g2)
    c: Coincident(g2,g3)
    c: Coincident(g3,g0)
    c: Horizontal(g0)
    c: Horizontal(g2)
    c: Vertical(g1)
    c: Vertical(g3)
    c: Coincident(g0,g-1)
    c: DistanceX(g2) = -270
    c: DistanceY(g3) = -4
FEATURE [PartDesign::Pad] Pad007
  Length = 4
  Length2 = 100
  Sketch = -> Sketch023
  Type = 0
FEATURE [Sketcher::SketchObject] Sketch024
  ExternalGeometry = -> [Pad007]
  Placement = pos=(0,274,0) rot=(0,0.707107,0.707107;3.14159rad)
  Support = -> Pad007 [Face3]
  sketch-geometry (4):
    g0: LineSegment StartX=-210 StartY=0 StartZ=0 EndX=-110 EndY=0 EndZ=0
    g1: LineSegment StartX=-110 StartY=0 StartZ=0 EndX=-110 EndY=4 EndZ=0
    g2: LineSegment StartX=-110 StartY=4 StartZ=0 EndX=-210 EndY=4 EndZ=0
    g3: LineSegment StartX=-210 StartY=4 StartZ=0 EndX=-210 EndY=0 EndZ=0
  constraints (12):
    c: Coincident(g0,g1)
    c: Coincident(g1,g2)
    c: Coincident(g2,g3)
    c: Coincident(g3,g0)
    c: Horizontal(g0)
    c: Horizontal(g2)
    c: Vertical(g1)
    c: Vertical(g3)
    c: DistanceX(g2) = -100
    c: DistanceY(g3) = -4
    c: DistanceX(g0,g-3) = -114
    c: DistanceY(g0,g-3) = 0
FEATURE [PartDesign::Pocket] Pocket012
  Length = 4
  Sketch = -> Sketch024
  Type = 0
FEATURE [Sketcher::SketchObject] Sketch025
  ExternalGeometry = -> [Pocket012]
  Placement = pos=(0,-4,0) rot=(1,0,0;1.5708rad)
  Support = -> Pocket012 [Face1]
  sketch-geometry (4):
    g0: LineSegment StartX=210 StartY=4 StartZ=0 EndX=110 EndY=4 EndZ=0
    g1: LineSegment StartX=110 StartY=4 StartZ=0 EndX=110 EndY=0 EndZ=0
    g2: LineSegment StartX=110 StartY=0 StartZ=0 EndX=210 EndY=0 EndZ=0
    g3: LineSegment StartX=210 StartY=0 StartZ=0 EndX=210 EndY=4 EndZ=0
  constraints (12):
    c: Coincident(g0,g1)
    c: Coincident(g1,g2)
    c: Coincident(g2,g3)
    c: Coincident(g3,g0)
    c: Horizontal(g0)
    c: Horizontal(g2)
    c: Vertical(g1)
    c: Vertical(g3)
    c: DistanceX(g0) = -100
    c: DistanceY(g3) = 4
    c: DistanceX(g2,g-3) = 114
    c: DistanceY(g2,g-3) = 0
FEATURE [PartDesign::Pocket] Pocket013
  Length = 4
  Sketch = -> Sketch025
  Type = 0
FEATURE [Sketcher::SketchObject] Sketch026
  ExternalGeometry = -> [Pocket013]
  Placement = pos=(324,0,0) rot=(0.57735,0.57735,0.57735;2.0944rad)
  Support = -> Pocket013 [Face1]
  sketch-geometry (4):
    g0: LineSegment StartX=185 StartY=4 StartZ=0 EndX=85 EndY=4 EndZ=0
    g1: LineSegment StartX=85 StartY=4 StartZ=0 EndX=85 EndY=0 EndZ=0
    g2: LineSegment StartX=85 StartY=0 StartZ=0 EndX=185 EndY=0 EndZ=0
    g3: LineSegment StartX=185 StartY=0 StartZ=0 EndX=185 EndY=4 EndZ=0
  constraints (12):
    c: Coincident(g0,g1)
    c: Coincident(g1,g2)
    c: Coincident(g2,g3)
    c: Coincident(g3,g0)
    c: Horizontal(g0)
    c: Horizontal(g2)
    c: Vertical(g1)
    c: Vertical(g3)
    c: DistanceX(g0) = -100
    c: DistanceY(g3) = 4
    c: DistanceX(g2,g-3) = 89
    c: DistanceY(g2,g-3) = 0
FEATURE [PartDesign::Pocket] Pocket014
  Length = 4
  Sketch = -> Sketch026
  Type = 0
FEATURE [Sketcher::SketchObject] Sketch027
  ExternalGeometry = -> [Pocket014]
  Placement = pos=(-4,0,0) rot=(0.57735,-0.57735,-0.57735;2.0944rad)
  Support = -> Pocket014 [Face6]
  sketch-geometry (4):
    g0: LineSegment StartX=-185 StartY=4 StartZ=0 EndX=-85 EndY=4 EndZ=0
    g1: LineSegment StartX=-85 StartY=4 StartZ=0 EndX=-85 EndY=0 EndZ=0
    g2: LineSegment StartX=-85 StartY=0 StartZ=0 EndX=-185 EndY=0 EndZ=0
    g3: LineSegment StartX=-185 StartY=0 StartZ=0 EndX=-185 EndY=4 EndZ=0
  constraints (12):
    c: Coincident(g0,g1)
    c: Coincident(g1,g2)
    c: Coincident(g2,g3)
    c: Coincident(g3,g0)
    c: Horizontal(g0)
    c: Horizontal(g2)
    c: Vertical(g1)
    c: Vertical(g3)
    c: DistanceX(g0) = 100
    c: DistanceY(g3) = 4
    c: DistanceX(g2,g-3) = -89
    c: DistanceY(g2,g-3) = 0
FEATURE [PartDesign::Pocket] Pocket015
  Length = 4
  Sketch = -> Sketch027
  Type = 0
FEATURE [Sketcher::SketchObject] Sketch028
  ExternalGeometry = -> [Pocket015]
  Placement = pos=(0,0,4) rot=(0,0,1;0rad)
  Support = -> Pocket015 [Face2]
  sketch-geometry (4):
    g0: Circle CenterX=4 CenterY=4 CenterZ=0 NormalX=0 NormalY=0 NormalZ=1 Radius=1.5
    g1: Circle CenterX=316 CenterY=4 CenterZ=0 NormalX=0 NormalY=0 NormalZ=1 Radius=1.5
    g2: Circle CenterX=316 CenterY=266 CenterZ=0 NormalX=0 NormalY=0 NormalZ=1 Radius=1.5
    g3: Circle CenterX=4 CenterY=266 CenterZ=0 NormalX=0 NormalY=0 NormalZ=1 Radius=1.5
  constraints (12):
    c: Radius(g0) = 1.5
    c: DistanceX(g0,g-3) = -8
    c: DistanceY(g0,g-3) = -8
    c: Radius(g1) = 1.5
    c: DistanceX(g1,g-4) = 8
    c: DistanceY(g1,g-4) = -8
    c: Radius(g2) = 1.5
    c: DistanceY(g2,g-5) = 8
    c: DistanceX(g2,g-5) = 8
    c: Radius(g3) = 1.5
    c: DistanceY(g-6,g3) = -8
    c: DistanceX(g3,g-6) = -8
FEATURE [PartDesign::Pocket] Pocket016  label="interFace-4mm(1)001"
  Length = 5
  Sketch = -> Sketch028
  Type = 0
